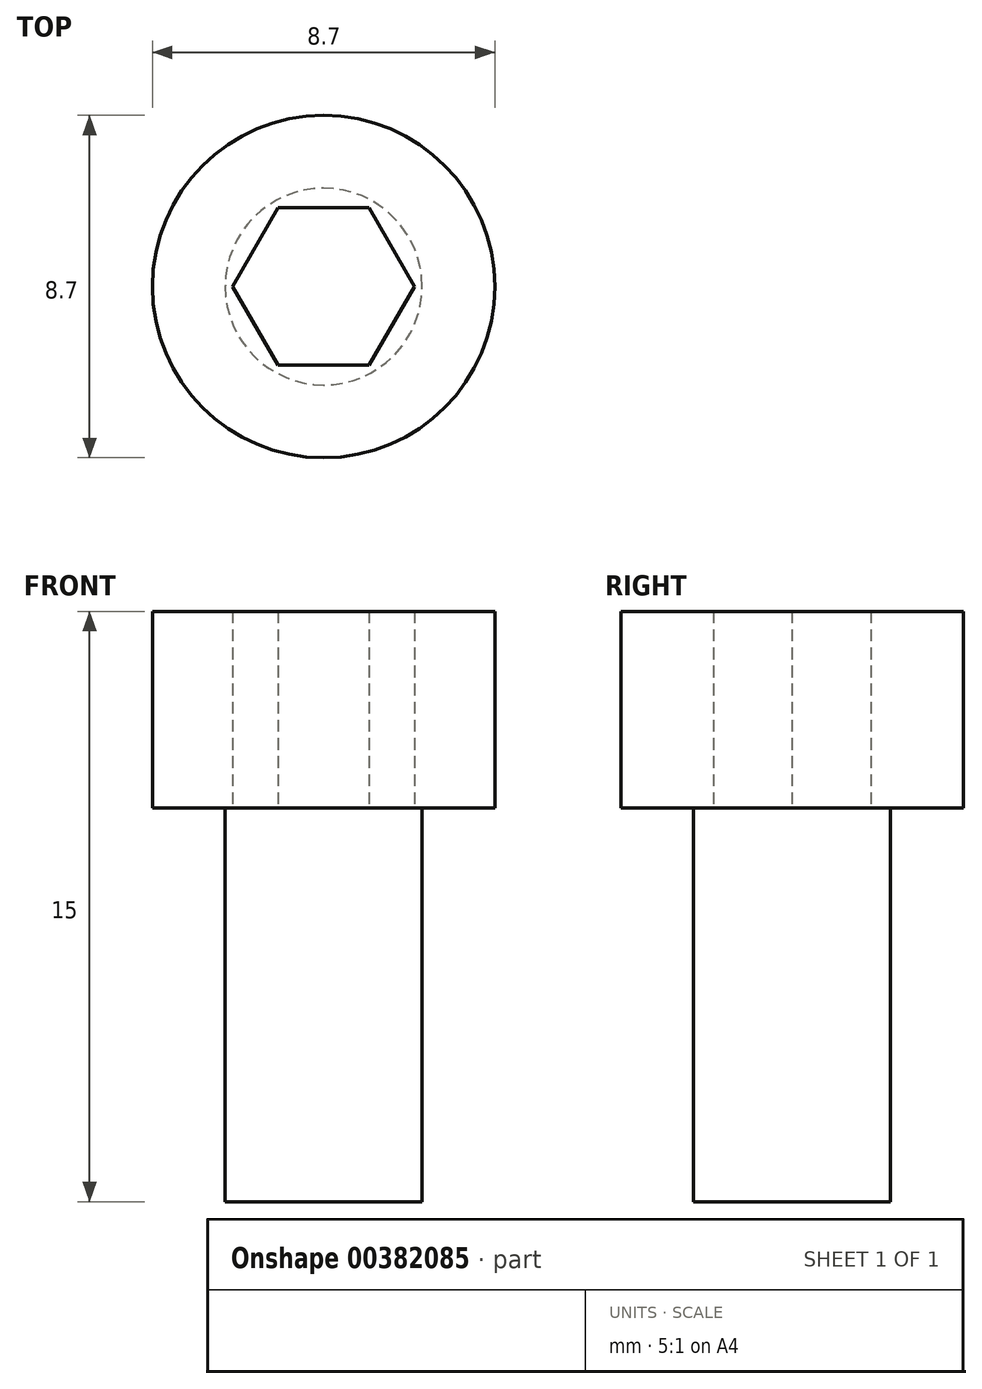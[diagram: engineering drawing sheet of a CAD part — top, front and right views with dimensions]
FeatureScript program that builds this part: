
annotation { "Feature Type Name" : "Feature", "Feature Type Description" : "" }
export const myFeature = defineFeature(function(context is Context, id is Id, definition is map)
    precondition{}
    {
        {
            var Q0;
            Q0=qCreatedBy(makeId("Top.planeOp"),FACE);
            var sketch = newSketch(context, id + "F0", { "sketchPlane" : qUnion([Q0])});
            skCircle(sketch, "E0", {"center": v(0, 0) * mm, "radius": 4.35 * mm});
            skCircle(sketch, "E1.cCircle", {"center": v(0, 0) * mm, "radius": 2 * mm, "construction": true});
            skLineSegment(sketch, "E1.0", {"start": v(1.15, -2) * mm, "end": v(-1.15, -2) * mm});
            skLineSegment(sketch, "E1.1", {"start": v(-1.15, -2) * mm, "end": v(-2.3, 0) * mm});
            skLineSegment(sketch, "E1.2", {"start": v(-2.3, 0) * mm, "end": v(-1.15, 2) * mm});
            skLineSegment(sketch, "E1.3", {"start": v(-1.15, 2) * mm, "end": v(1.15, 2) * mm});
            skLineSegment(sketch, "E1.4", {"start": v(1.15, 2) * mm, "end": v(2.3, 0) * mm});
            skLineSegment(sketch, "E1.5", {"start": v(2.3, 0) * mm, "end": v(1.15, -2) * mm});
            skPoint(sketch, "E1.0.midPoint", {"position": v(0, -2) * mm});
            skCircle(sketch, "E2", {"center": v(0, 0) * mm, "radius": 2.5 * mm});
            skSolve(sketch);
        }
        {
            var Q0;
            Q0=makeQuery(id+"F0.imprint","IMPRINT",FACE,{"disambiguationData":[TD([[makeQuery(id+"F0.imprint","IMPRINT",EDGE,{"derivedFrom":sQuery(id+"F0.wireOp",EDGE,"E1.0")}),1.0]])]});
            var Q1;
            Q1=makeQuery(id+"F0.imprint","IMPRINT",FACE,{"disambiguationData":[TD([[makeQuery(id+"F0.imprint","IMPRINT",EDGE,{"derivedFrom":sQuery(id+"F0.wireOp",EDGE,"E1.0")}),-1.0]])]});
            extrude(context, id + "F1", {"entities" : qUnion([Q0, Q1]), "oppositeDirection" : true, "depth" : 10 * mm});
        }
        {
            var Q0;
            Q0=makeQuery(id+"F0.imprint","IMPRINT",FACE,{"disambiguationData":[TD([[makeQuery(id+"F0.imprint","IMPRINT",EDGE,{"derivedFrom":sQuery(id+"F0.wireOp",EDGE,"E0")}),1.0]])]});
            var Q1;
            Q1=makeQuery(id+"F0.imprint","IMPRINT",FACE,{"disambiguationData":[TD([[makeQuery(id+"F0.imprint","IMPRINT",EDGE,{"derivedFrom":sQuery(id+"F0.wireOp",EDGE,"E1.0")}),1.0]])]});
            extrude(context, id + "F2", {"entities" : qUnion([Q0, Q1]), "operationType" : NewBodyOperationType.ADD, "depth" : 5 * mm});
        }
    });
